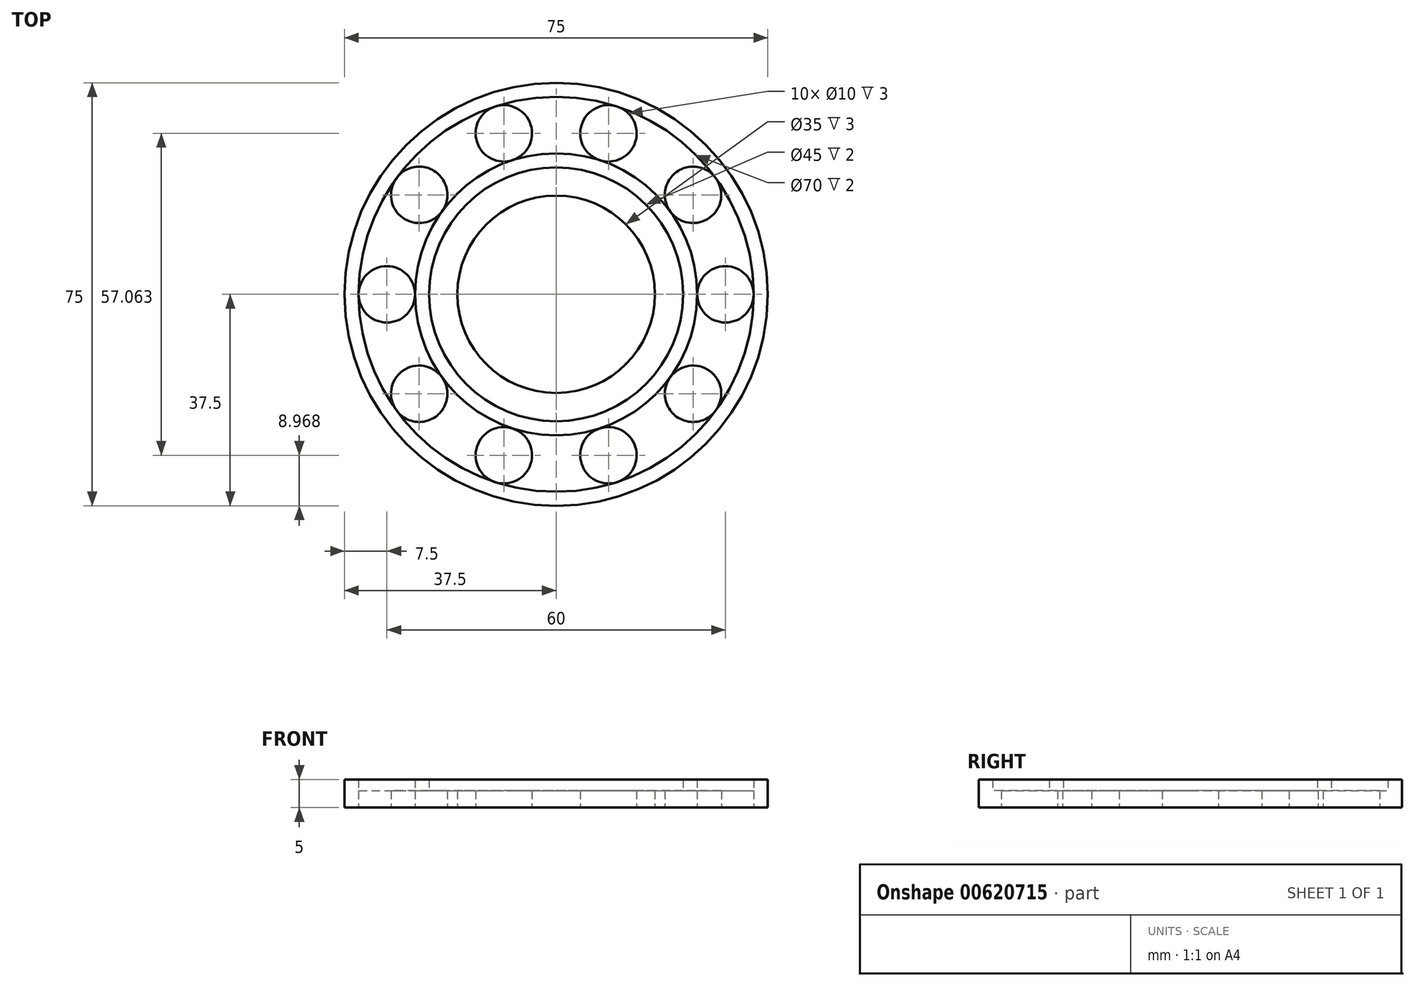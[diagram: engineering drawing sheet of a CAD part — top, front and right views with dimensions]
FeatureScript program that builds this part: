
annotation { "Feature Type Name" : "Feature", "Feature Type Description" : "" }
export const myFeature = defineFeature(function(context is Context, id is Id, definition is map)
    precondition{}
    {
        {
            var Q0;
            Q0=qCreatedBy(makeId("Top.planeOp"),FACE);
            var sketch = newSketch(context, id + "F0", { "sketchPlane" : qUnion([Q0])});
            skCircle(sketch, "E0", {"center": v(0, 0) * mm, "radius": 22.5 * mm});
            skCircle(sketch, "E1", {"center": v(0, 0) * mm, "radius": 17.5 * mm});
            skCircle(sketch, "E2", {"center": v(0, 0) * mm, "radius": 25 * mm});
            skCircle(sketch, "E3", {"center": v(0, 0) * mm, "radius": 35 * mm});
            skCircle(sketch, "E4", {"center": v(0, 0) * mm, "radius": 37.5 * mm});
            skLineSegment(sketch, "E5", {"start": v(0, 0) * mm, "end": v(30, 0) * mm});
            skCircle(sketch, "E6", {"center": v(30, 0) * mm, "radius": 5 * mm});
            skCircle(sketch, "E7.1.0", {"center": v(24.27, 17.63) * mm, "radius": 5 * mm});
            skCircle(sketch, "E7.2.0", {"center": v(9.27, 28.53) * mm, "radius": 5 * mm});
            skCircle(sketch, "E7.3.0", {"center": v(-9.27, 28.53) * mm, "radius": 5 * mm});
            skCircle(sketch, "E7.4.0", {"center": v(-24.27, 17.63) * mm, "radius": 5 * mm});
            skCircle(sketch, "E7.5.0", {"center": v(-30, 0) * mm, "radius": 5 * mm});
            skCircle(sketch, "E7.6.0", {"center": v(-24.27, -17.63) * mm, "radius": 5 * mm});
            skCircle(sketch, "E7.7.0", {"center": v(-9.27, -28.53) * mm, "radius": 5 * mm});
            skCircle(sketch, "E7.8.0", {"center": v(9.27, -28.53) * mm, "radius": 5 * mm});
            skCircle(sketch, "E7.9.0", {"center": v(24.27, -17.63) * mm, "radius": 5 * mm});
            skSolve(sketch);
        }
        {
            var Q0;
            Q0=makeQuery(id+"F0.imprint","IMPRINT",FACE,{"disambiguationData":[TD([[makeQuery(id+"F0.imprint","IMPRINT",EDGE,{"derivedFrom":sQuery(id+"F0.wireOp",EDGE,"E4")}),1.0]])]});
            var Q1;
            {var subQ0=sQuery(id+"F0.wireOp",EDGE,"E7.7.0");var subQ1=sQuery(id+"F0.wireOp",EDGE,"E2");var subQ2=makeQuery(id+"F0.imprint","INTERSECT",VERTEX,{"derivedFrom":[subQ1,subQ0]});Q1=makeQuery(id+"F0.imprint","IMPRINT",FACE,{"disambiguationData":[TD([[makeQuery(id+"F0.imprint","IMPRINT",EDGE,{"disambiguationData":[TD([[subQ2,-1.0]])],"derivedFrom":subQ1}),-1.0]])]});}
            var Q2;
            {var subQ0=sQuery(id+"F0.wireOp",EDGE,"E7.8.0");var subQ1=sQuery(id+"F0.wireOp",EDGE,"E2");var subQ2=makeQuery(id+"F0.imprint","INTERSECT",VERTEX,{"derivedFrom":[subQ1,subQ0]});Q2=makeQuery(id+"F0.imprint","IMPRINT",FACE,{"disambiguationData":[TD([[makeQuery(id+"F0.imprint","IMPRINT",EDGE,{"disambiguationData":[TD([[subQ2,-1.0]])],"derivedFrom":subQ1}),-1.0]])]});}
            var Q3;
            {var subQ0=sQuery(id+"F0.wireOp",EDGE,"E6");var subQ1=sQuery(id+"F0.wireOp",EDGE,"E2");var subQ2=makeQuery(id+"F0.imprint","INTERSECT",VERTEX,{"derivedFrom":[subQ1,subQ0]});Q3=makeQuery(id+"F0.imprint","IMPRINT",FACE,{"disambiguationData":[TD([[makeQuery(id+"F0.imprint","IMPRINT",EDGE,{"disambiguationData":[TD([[subQ2,1.0]])],"derivedFrom":subQ1}),-1.0]])]});}
            var Q4;
            {var subQ0=sQuery(id+"F0.wireOp",EDGE,"E7.1.0");var subQ1=sQuery(id+"F0.wireOp",EDGE,"E2");var subQ2=makeQuery(id+"F0.imprint","INTERSECT",VERTEX,{"derivedFrom":[subQ1,subQ0]});Q4=makeQuery(id+"F0.imprint","IMPRINT",FACE,{"disambiguationData":[TD([[makeQuery(id+"F0.imprint","IMPRINT",EDGE,{"disambiguationData":[TD([[subQ2,1.0]])],"derivedFrom":subQ1}),-1.0]])]});}
            var Q5;
            {var subQ0=sQuery(id+"F0.wireOp",EDGE,"E7.1.0");var subQ1=sQuery(id+"F0.wireOp",EDGE,"E2");var subQ2=makeQuery(id+"F0.imprint","INTERSECT",VERTEX,{"derivedFrom":[subQ1,subQ0]});Q5=makeQuery(id+"F0.imprint","IMPRINT",FACE,{"disambiguationData":[TD([[makeQuery(id+"F0.imprint","IMPRINT",EDGE,{"disambiguationData":[TD([[subQ2,-1.0]])],"derivedFrom":subQ1}),-1.0]])]});}
            var Q6;
            {var subQ0=sQuery(id+"F0.wireOp",EDGE,"E7.2.0");var subQ1=sQuery(id+"F0.wireOp",EDGE,"E2");var subQ2=makeQuery(id+"F0.imprint","INTERSECT",VERTEX,{"derivedFrom":[subQ1,subQ0]});Q6=makeQuery(id+"F0.imprint","IMPRINT",FACE,{"disambiguationData":[TD([[makeQuery(id+"F0.imprint","IMPRINT",EDGE,{"disambiguationData":[TD([[subQ2,-1.0]])],"derivedFrom":subQ1}),-1.0]])]});}
            var Q7;
            {var subQ0=sQuery(id+"F0.wireOp",EDGE,"E7.3.0");var subQ1=sQuery(id+"F0.wireOp",EDGE,"E2");var subQ2=makeQuery(id+"F0.imprint","INTERSECT",VERTEX,{"derivedFrom":[subQ1,subQ0]});Q7=makeQuery(id+"F0.imprint","IMPRINT",FACE,{"disambiguationData":[TD([[makeQuery(id+"F0.imprint","IMPRINT",EDGE,{"disambiguationData":[TD([[subQ2,-1.0]])],"derivedFrom":subQ1}),-1.0]])]});}
            var Q8;
            {var subQ0=sQuery(id+"F0.wireOp",EDGE,"E7.4.0");var subQ1=sQuery(id+"F0.wireOp",EDGE,"E2");var subQ2=makeQuery(id+"F0.imprint","INTERSECT",VERTEX,{"derivedFrom":[subQ1,subQ0]});Q8=makeQuery(id+"F0.imprint","IMPRINT",FACE,{"disambiguationData":[TD([[makeQuery(id+"F0.imprint","IMPRINT",EDGE,{"disambiguationData":[TD([[subQ2,-1.0]])],"derivedFrom":subQ1}),-1.0]])]});}
            var Q9;
            {var subQ0=sQuery(id+"F0.wireOp",EDGE,"E7.6.0");var subQ1=sQuery(id+"F0.wireOp",EDGE,"E2");var subQ2=makeQuery(id+"F0.imprint","INTERSECT",VERTEX,{"derivedFrom":[subQ1,subQ0]});Q9=makeQuery(id+"F0.imprint","IMPRINT",FACE,{"disambiguationData":[TD([[makeQuery(id+"F0.imprint","IMPRINT",EDGE,{"disambiguationData":[TD([[subQ2,-1.0]])],"derivedFrom":subQ1}),-1.0]])]});}
            var Q10;
            {var subQ0=sQuery(id+"F0.wireOp",EDGE,"E7.5.0");var subQ1=sQuery(id+"F0.wireOp",EDGE,"E2");var subQ2=makeQuery(id+"F0.imprint","INTERSECT",VERTEX,{"derivedFrom":[subQ1,subQ0]});Q10=makeQuery(id+"F0.imprint","IMPRINT",FACE,{"disambiguationData":[TD([[makeQuery(id+"F0.imprint","IMPRINT",EDGE,{"disambiguationData":[TD([[subQ2,-1.0]])],"derivedFrom":subQ1}),-1.0]])]});}
            var Q11;
            Q11=makeQuery(id+"F0.imprint","IMPRINT",FACE,{"disambiguationData":[TD([[makeQuery(id+"F0.imprint","IMPRINT",EDGE,{"derivedFrom":sQuery(id+"F0.wireOp",EDGE,"E0")}),1.0]])]});
            var Q12;
            Q12=makeQuery(id+"F0.imprint","IMPRINT",FACE,{"disambiguationData":[TD([[makeQuery(id+"F0.imprint","IMPRINT",EDGE,{"derivedFrom":sQuery(id+"F0.wireOp",EDGE,"E0")}),-1.0]])]});
            extrude(context, id + "F1", {"entities" : qUnion([Q0, Q1, Q2, Q3, Q4, Q5, Q6, Q7, Q8, Q9, Q10, Q11, Q12]), "depth" : 3 * mm, "offsetDistance" : 25 * mm});
        }
        {
            var Q0;
            Q0=makeQuery(id+"F0.imprint","IMPRINT",FACE,{"disambiguationData":[TD([[makeQuery(id+"F0.imprint","IMPRINT",EDGE,{"derivedFrom":sQuery(id+"F0.wireOp",EDGE,"E0")}),-1.0]])]});
            var Q1;
            Q1=makeQuery(id+"F0.imprint","IMPRINT",FACE,{"disambiguationData":[TD([[makeQuery(id+"F0.imprint","IMPRINT",EDGE,{"derivedFrom":sQuery(id+"F0.wireOp",EDGE,"E4")}),1.0]])]});
            extrude(context, id + "F2", {"entities" : qUnion([Q0, Q1]), "operationType" : NewBodyOperationType.ADD, "depth" : 5 * mm, "offsetDistance" : 25 * mm});
        }
    });
